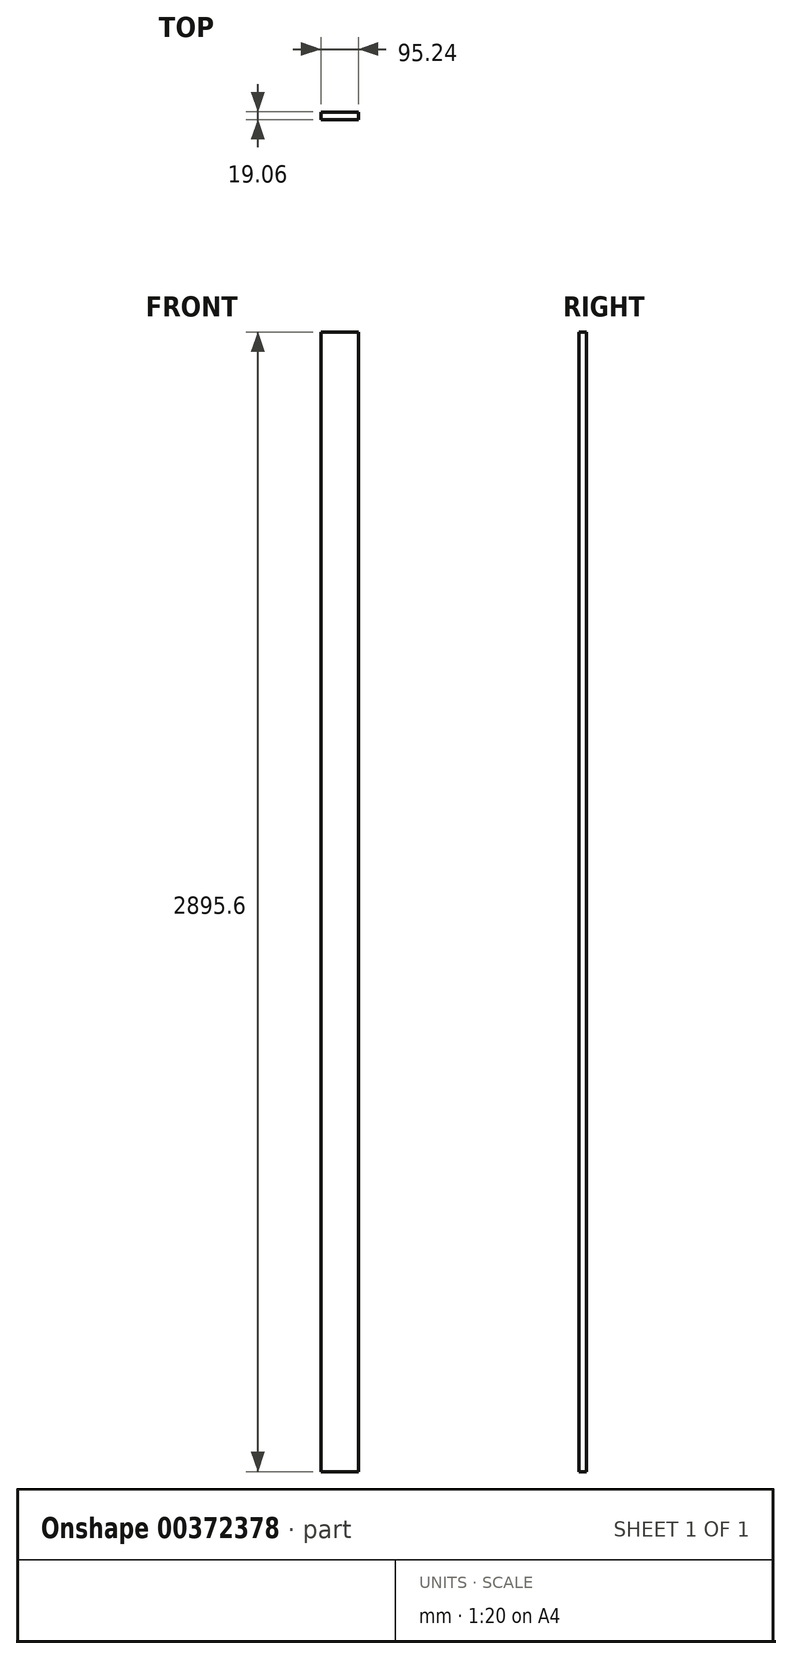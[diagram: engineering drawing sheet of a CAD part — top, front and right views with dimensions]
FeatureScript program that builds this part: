
annotation { "Feature Type Name" : "Feature", "Feature Type Description" : "" }
export const myFeature = defineFeature(function(context is Context, id is Id, definition is map)
    precondition{}
    {
        {
            var Q0;
            Q0=qCreatedBy(makeId("Top.planeOp"),FACE);
            var sketch = newSketch(context, id + "F0", { "sketchPlane" : qUnion([Q0])});
            skLineSegment(sketch, "E0.bottom", {"start": v(-47.62, 9.53) * mm, "end": v(47.63, 9.53) * mm});
            skLineSegment(sketch, "E0.top", {"start": v(-47.62, -9.53) * mm, "end": v(47.63, -9.53) * mm});
            skLineSegment(sketch, "E0.left", {"start": v(-47.62, 9.53) * mm, "end": v(-47.62, -9.52) * mm});
            skLineSegment(sketch, "E0.right", {"start": v(47.63, 9.53) * mm, "end": v(47.63, -9.52) * mm});
            skPoint(sketch, "E0.middle", {"position": v(0, 0) * mm});
            skSolve(sketch);
        }
        {
            var Q0;
            Q0=qSketchRegion(id+"F0",true);
            extrude(context, id + "F1", {"entities" : qUnion([Q0]), "endBound" : BoundingType.SYMMETRIC, "depth" : 2895.6 * mm});
        }
    });
